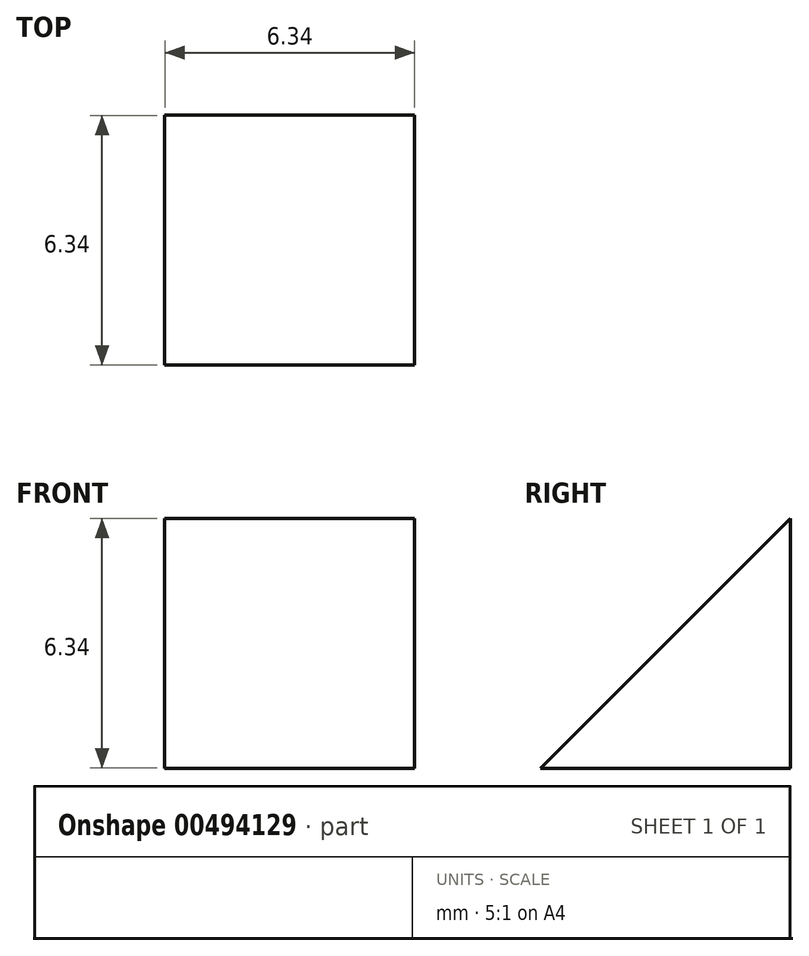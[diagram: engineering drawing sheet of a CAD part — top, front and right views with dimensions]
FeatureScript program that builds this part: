
annotation { "Feature Type Name" : "Feature", "Feature Type Description" : "" }
export const myFeature = defineFeature(function(context is Context, id is Id, definition is map)
    precondition{}
    {
        {
            var Q0;
            Q0=qCreatedBy(makeId("Right.planeOp"),FACE);
            var sketch = newSketch(context, id + "F0", { "sketchPlane" : qUnion([Q0])});
            skLineSegment(sketch, "E0.top", {"start": v(-3.17, -3.18) * mm, "end": v(3.18, -3.18) * mm});
            skLineSegment(sketch, "E0.right", {"start": v(3.18, 3.17) * mm, "end": v(3.18, -3.18) * mm});
            skPoint(sketch, "E0.middle", {"position": v(0, 0) * mm});
            skLineSegment(sketch, "E1", {"start": v(3.18, 3.17) * mm, "end": v(-3.17, -3.18) * mm});
            skSolve(sketch);
        }
        {
            var Q0;
            Q0=makeQuery(id+"F0.imprint","IMPRINT",FACE,{"disambiguationData":[TD([[makeQuery(id+"F0.imprint","IMPRINT",EDGE,{"derivedFrom":sQuery(id+"F0.wireOp",EDGE,"E0.bottom")}),-1.0]])]});
            var Q1;
            Q1=makeQuery(id+"F0.imprint","IMPRINT",FACE,{"disambiguationData":[TD([[makeQuery(id+"F0.imprint","IMPRINT",EDGE,{"derivedFrom":sQuery(id+"F0.wireOp",EDGE,"E0.top")}),1.0]])]});
            extrude(context, id + "F1", {"entities" : qUnion([Q0, Q1]), "endBound" : BoundingType.SYMMETRIC, "depth" : 6.35 * mm});
        }
    });
